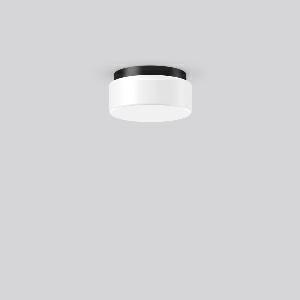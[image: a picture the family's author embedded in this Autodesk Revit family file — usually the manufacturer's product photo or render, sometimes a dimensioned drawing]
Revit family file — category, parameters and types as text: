
# Revit family: kreis_21101_003_5cd7
name_source: partatom
category: Lighting Fixtures
units: mm (PartAtom-declared; Revit-internal decimal feet)

## family parameters
Cut with Voids When Loaded = No
Host = Face
Light Source = No
Part Type = Normal
Room Calculation Point = No
Round Connector Dimension = Use Diameter
Shared = No

## types (1)
- KREIS (1 x QA60/clear E27, 915 lm, 57 W, 3000)
    Apparent Load = 57 VA
    CIE Flux Codes = 34 63 85 71 62
    Color Rendering = 90
    Color Temperature = 3000
    Default Elevation = 1800 mm
    Description = Series: KREIS
Round surface-mounted luminaire in classic design. Base: plastic. Opal glass: mouth-blown, satin finish. Diffuser fastening: spring system. Suitable for Ceiling mounting, Wall (surface). IP 43 ceiling mounting, IP 44 wall mounting. 
Colour: black
Diameter: 230 mm
Height: 110 mm
Lamp: A60
Number of lamps: 1
Wattage: 75 W
Socket: E27
System power: 57 W
Rated luminous flux: 570 lm
Luminous efficiency: 10 lm/W
Control gear: Converter not necessary
Protection class: II
Type of protection: IP 43
    Height = 110 mm
    Lamp = 1 x QA60/clear E27
    Lamp Light Flux = 915 lm
    Lamp Power = 57 W
    Lamp count = 1
    Length = 230 mm
    Lifetime = 3000 h
    Luminous efficacy = 10 lm/W
    Manufacturer = RZB
    ModVariant = No
    Model = 21101.003
    Mounting Place = Ceiling, Wall
    Mounting Type = Surface mounted
    Number of Poles = 1
    OnlyDefault = Yes
    Power Factor = 1
    Product Name = KREIS
    Product group = Surface mounted ceiling and wall luminaires
    ProductGroupID = 305
    Protection Class = Protection class II
    Protection Degree = IP 43
    RLX_Detail_Level = 1
    RLX_Emergency_Light_Flux = 0 lm
    RLX_Emergency_Type = 0
    RLX_Emergency_Type_DB = No
    RlxData = <blob elided: 11865 chars, md5=f4f56dea>
    Socket = E27
    Standby Power = 0 W
    System Light Flux = 565 lm
    System Power = 57 W
    Type Comments = Product without accessories
    Type Image = 21101.003.jpg
    URL = http://relux.com
    VarID = ---
    Voltage = 230 V
    Voltage Range = 220-240 V
    Weight = 0.00 kg
    Width = 0 mm  [stored 0 ft]

note: [stored X ft] marks values corroborated as IEEE doubles in the binary element streams (Revit-internal decimal feet)

## geometry (parser evidence)
native form markers: Sweep x11
no freeform markers — native parametric forms only
